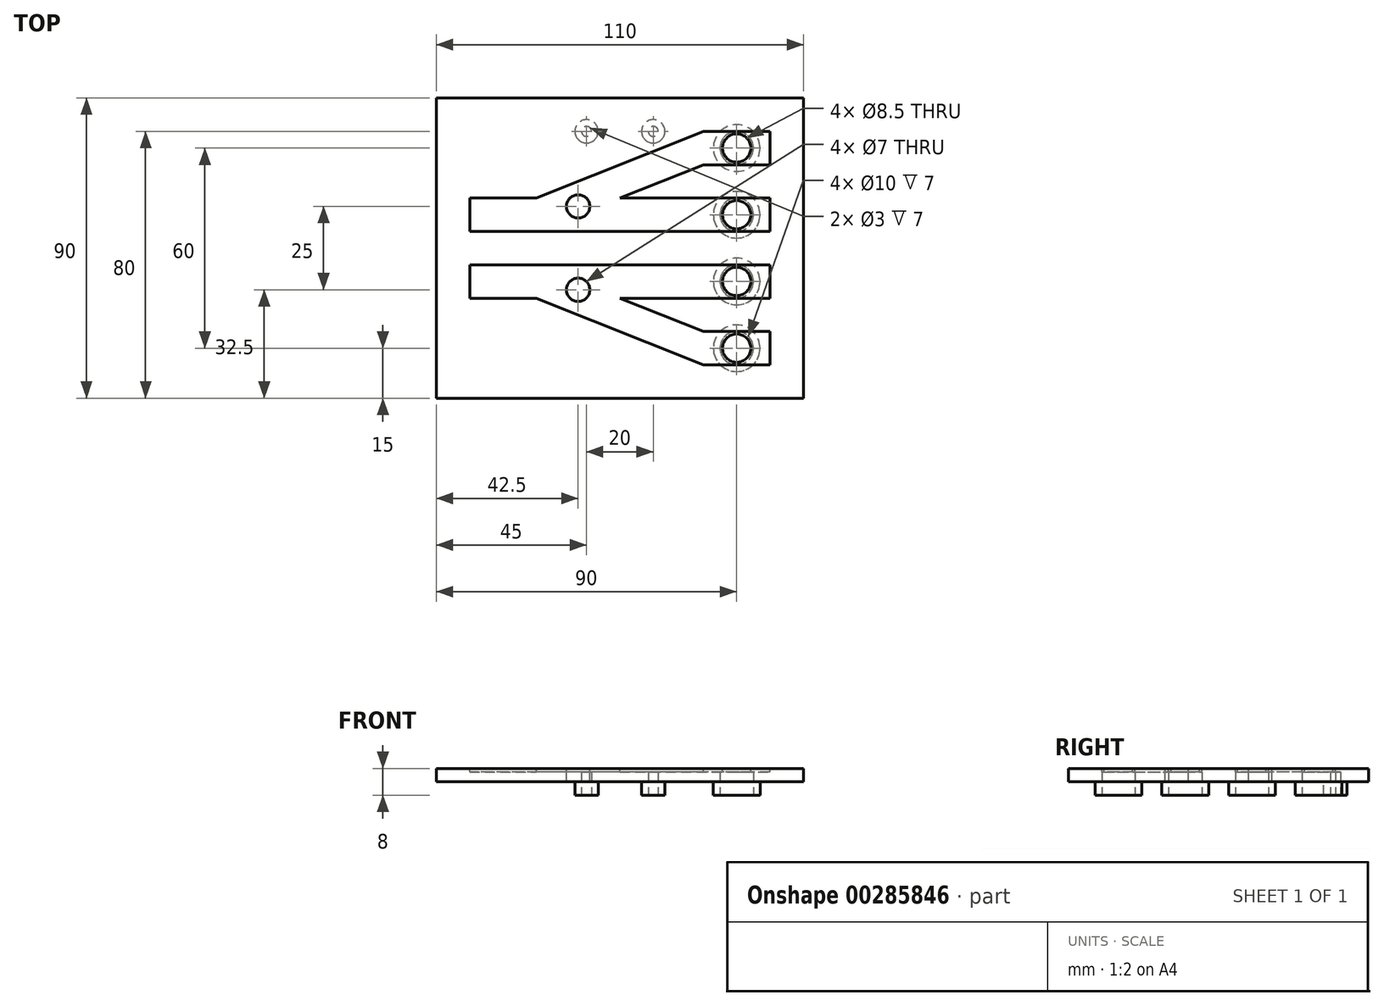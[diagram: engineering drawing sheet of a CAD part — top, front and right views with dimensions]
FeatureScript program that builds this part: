
annotation { "Feature Type Name" : "Feature", "Feature Type Description" : "" }
export const myFeature = defineFeature(function(context is Context, id is Id, definition is map)
    precondition{}
    {
        {
            var Q0;
            Q0=qCreatedBy(makeId("Top.planeOp"),FACE);
            var sketch = newSketch(context, id + "F0", { "sketchPlane" : qUnion([Q0])});
            skLineSegment(sketch, "E0.bottom", {"start": v(55, -45) * mm, "end": v(-55, -45) * mm});
            skLineSegment(sketch, "E0.top", {"start": v(55, 45) * mm, "end": v(-55, 45) * mm});
            skLineSegment(sketch, "E0.left", {"start": v(55, -45) * mm, "end": v(55, 45) * mm});
            skLineSegment(sketch, "E0.right", {"start": v(-55, -45) * mm, "end": v(-55, 45) * mm});
            skPoint(sketch, "E0.middle", {"position": v(0, 0) * mm});
            skSolve(sketch);
        }
        {
            var Q0;
            Q0 = qSketchRegion(id + "F0", true);
            extrude(context, id + "F1", {"entities" : qUnion([Q0]), "oppositeDirection" : true, "depth" : 4 * mm});
        }
        {
            var Q0;
            Q0=makeQuery(id+"F1.opExtrude","CAP_FACE",FACE,{"disambiguationData":[OSD([sQuery(id+"F0.wireOp",EDGE,"E0.bottom"),sQuery(id+"F0.wireOp",EDGE,"E0.top"),sQuery(id+"F0.wireOp",EDGE,"E0.left"),sQuery(id+"F0.wireOp",EDGE,"E0.right")])],"isStart":false});
            cPlane(context, id + "F2", {"entities" : qUnion([Q0]), "cplaneType" : CPlaneType.OFFSET, "offset" : 0 * mm, "width" : 150 * mm, "height" : 150 * mm});
        }
        {
            var Q0;
            Q0=qCreatedBy(makeId("Top.planeOp"),FACE);
            var sketch = newSketch(context, id + "F3", { "sketchPlane" : qUnion([Q0])});
            skLineSegment(sketch, "E1.bottom", {"start": v(-45, 15) * mm, "end": v(-25, 15) * mm});
            skLineSegment(sketch, "E1.left", {"start": v(-45, 15) * mm, "end": v(-45, 5) * mm});
            skLineSegment(sketch, "E1.right", {"start": v(45, 15) * mm, "end": v(45, 5) * mm});
            skLineSegment(sketch, "E2.bottom", {"start": v(45, 25) * mm, "end": v(25, 25) * mm});
            skLineSegment(sketch, "E2.top", {"start": v(45, 35) * mm, "end": v(25, 35) * mm});
            skLineSegment(sketch, "E2.left", {"start": v(45, 25) * mm, "end": v(45, 35) * mm});
            skLineSegment(sketch, "E3", {"start": v(25, 35) * mm, "end": v(-25, 15) * mm});
            skPoint(sketch, "E4.endSnap0", {"position": v(0, 25) * mm});
            skLineSegment(sketch, "E5", {"start": v(0, 15) * mm, "end": v(45, 15) * mm});
            skLineSegment(sketch, "E6", {"start": v(45, 5) * mm, "end": v(-45, 5) * mm});
            skPoint(sketch, "E7.startSnap0", {"position": v(0, 5) * mm});
            skLineSegment(sketch, "E8", {"start": v(25, 25) * mm, "end": v(0, 15) * mm});
            skPoint(sketch, "E9.centerSnap0", {"position": v(35, 35) * mm});
            skPoint(sketch, "E9.centerSnap1", {"position": v(45, 30) * mm});
            skPoint(sketch, "E10", {"position": v(45, 10) * mm});
            skLineSegment(sketch, "E11.MirrorCS", {"start": v(25, -25) * mm, "end": v(0, -15) * mm});
            skLineSegment(sketch, "E12.MirrorCS", {"start": v(45, -15) * mm, "end": v(45, -5) * mm});
            skLineSegment(sketch, "E13.MirrorCS", {"start": v(45, -35) * mm, "end": v(25, -35) * mm});
            skLineSegment(sketch, "E14.MirrorCS", {"start": v(-45, -15) * mm, "end": v(-25, -15) * mm});
            skLineSegment(sketch, "E15.MirrorCS", {"start": v(-45, -15) * mm, "end": v(-45, -5) * mm});
            skPoint(sketch, "E16.MirrorP", {"position": v(45, -30) * mm});
            skPoint(sketch, "E17.MirrorP", {"position": v(0, -25) * mm});
            skLineSegment(sketch, "E18.MirrorCS", {"start": v(45, -25) * mm, "end": v(25, -25) * mm});
            skLineSegment(sketch, "E19.MirrorCS", {"start": v(25, -35) * mm, "end": v(-25, -15) * mm});
            skLineSegment(sketch, "E20.MirrorCS", {"start": v(0, -15) * mm, "end": v(45, -15) * mm});
            skLineSegment(sketch, "E21.MirrorCS", {"start": v(45, -25) * mm, "end": v(45, -35) * mm});
            skLineSegment(sketch, "E22.MirrorCS", {"start": v(45, -5) * mm, "end": v(-45, -5) * mm});
            skPoint(sketch, "E23.MirrorP", {"position": v(0, -5) * mm});
            skPoint(sketch, "E24.MirrorP", {"position": v(45, -10) * mm});
            skPoint(sketch, "E25.MirrorP", {"position": v(35, -35) * mm});
            skSolve(sketch);
        }
        {
            var Q0;
            Q0=qCreatedBy(makeId("Top.planeOp"),FACE);
            var sketch = newSketch(context, id + "F4", { "sketchPlane" : qUnion([Q0])});
            skLineSegment(sketch, "E26.0.0", {"start": v(25, 25) * mm, "end": v(45, 25) * mm, "construction": true});
            skLineSegment(sketch, "E26.0.1", {"start": v(45, 25) * mm, "end": v(45, 35) * mm, "construction": true});
            skLineSegment(sketch, "E26.0.2", {"start": v(45, 35) * mm, "end": v(25, 35) * mm, "construction": true});
            skLineSegment(sketch, "E26.0.3", {"start": v(25, 35) * mm, "end": v(-25, 15) * mm, "construction": true});
            skLineSegment(sketch, "E26.0.4", {"start": v(-25, 15) * mm, "end": v(-45, 15) * mm, "construction": true});
            skLineSegment(sketch, "E26.0.5", {"start": v(-45, 15) * mm, "end": v(-45, 5) * mm, "construction": true});
            skLineSegment(sketch, "E26.0.6", {"start": v(-45, 5) * mm, "end": v(45, 5) * mm, "construction": true});
            skLineSegment(sketch, "E26.0.7", {"start": v(45, 5) * mm, "end": v(45, 15) * mm, "construction": true});
            skLineSegment(sketch, "E26.0.8", {"start": v(45, 15) * mm, "end": v(0, 15) * mm, "construction": true});
            skLineSegment(sketch, "E26.0.9", {"start": v(0, 15) * mm, "end": v(25, 25) * mm, "construction": true});
            skLineSegment(sketch, "E27.0.0", {"start": v(-45, -5) * mm, "end": v(-45, -15) * mm, "construction": true});
            skLineSegment(sketch, "E27.0.1", {"start": v(-45, -15) * mm, "end": v(-25, -15) * mm, "construction": true});
            skLineSegment(sketch, "E27.0.2", {"start": v(-25, -15) * mm, "end": v(25, -35) * mm, "construction": true});
            skLineSegment(sketch, "E27.0.3", {"start": v(25, -35) * mm, "end": v(45, -35) * mm, "construction": true});
            skLineSegment(sketch, "E27.0.4", {"start": v(45, -35) * mm, "end": v(45, -25) * mm, "construction": true});
            skLineSegment(sketch, "E27.0.5", {"start": v(45, -25) * mm, "end": v(25, -25) * mm, "construction": true});
            skLineSegment(sketch, "E27.0.6", {"start": v(25, -25) * mm, "end": v(0, -15) * mm, "construction": true});
            skLineSegment(sketch, "E27.0.7", {"start": v(0, -15) * mm, "end": v(45, -15) * mm, "construction": true});
            skLineSegment(sketch, "E27.0.8", {"start": v(45, -15) * mm, "end": v(45, -5) * mm, "construction": true});
            skLineSegment(sketch, "E27.0.9", {"start": v(45, -5) * mm, "end": v(-45, -5) * mm, "construction": true});
            skLineSegment(sketch, "E28", {"start": v(-25, 15) * mm, "end": v(0, 15) * mm, "construction": true});
            skLineSegment(sketch, "E29", {"start": v(-12.5, 5) * mm, "end": v(-12.5, 20) * mm, "construction": true});
            skPoint(sketch, "E29.startSnap0", {"position": v(-12.5, 15) * mm});
            skCircle(sketch, "E30", {"center": v(-12.5, 12.5) * mm, "radius": 3.5 * mm});
            skCircle(sketch, "E31", {"center": v(35, 30) * mm, "radius": 4.25 * mm});
            skPoint(sketch, "E31.centerSnap0", {"position": v(45, 30) * mm});
            skPoint(sketch, "E31.centerSnap1", {"position": v(35, 35) * mm});
            skCircle(sketch, "E32", {"center": v(35, 10) * mm, "radius": 4.25 * mm});
            skPoint(sketch, "E32.centerSnap0", {"position": v(45, 10) * mm});
            skPoint(sketch, "E32.centerSnap1", {"position": v(35, 25) * mm});
            skCircle(sketch, "E33.MirrorC", {"center": v(35, -10) * mm, "radius": 4.25 * mm});
            skCircle(sketch, "E34.MirrorC", {"center": v(35, -30) * mm, "radius": 4.25 * mm});
            skCircle(sketch, "E35.MirrorC", {"center": v(-12.5, -12.5) * mm, "radius": 3.5 * mm});
            skSolve(sketch);
        }
        {
            var Q0;
            Q0 = qSketchRegion(id + "F3", true);
            extrude(context, id + "F5", {"entities" : qUnion([Q0]), "operationType" : NewBodyOperationType.REMOVE, "oppositeDirection" : true, "depth" : 1 * mm});
        }
        {
            var Q0;
            Q0 = qSketchRegion(id + "F3", true);
            extrude(context, id + "F6", {"entities" : qUnion([Q0]), "oppositeDirection" : true, "depth" : 1 * mm});
        }
        {
            var Q0;
            Q0 = qSketchRegion(id + "F4", true);
            var Q1;
            Q1=makeQuery(id+"F1.opExtrude","CAP_FACE",FACE,{"disambiguationData":[OSD([sQuery(id+"F0.wireOp",EDGE,"E0.bottom"),sQuery(id+"F0.wireOp",EDGE,"E0.top"),sQuery(id+"F0.wireOp",EDGE,"E0.left"),sQuery(id+"F0.wireOp",EDGE,"E0.right")])],"isStart":false});
            extrude(context, id + "F7", {"entities" : qUnion([Q0]), "operationType" : NewBodyOperationType.REMOVE, "endBound" : BoundingType.UP_TO_SURFACE, "oppositeDirection" : true, "endBoundEntityFace" : qUnion([Q1]), "depth" : 25 * mm});
        }
        {
            var Q0;
            Q0=qCreatedBy(id+"F2.planeOp",FACE);
            var sketch = newSketch(context, id + "F8", { "sketchPlane" : qUnion([Q0])});
            skCircle(sketch, "E36.0", {"center": v(35, -30) * mm, "radius": 4.25 * mm, "construction": true});
            skCircle(sketch, "E37.0", {"center": v(35, -10) * mm, "radius": 4.25 * mm, "construction": true});
            skCircle(sketch, "E38.0", {"center": v(35, 10) * mm, "radius": 4.25 * mm, "construction": true});
            skCircle(sketch, "E39.0", {"center": v(35, 30) * mm, "radius": 4.25 * mm, "construction": true});
            skCircle(sketch, "E40", {"center": v(35, -30) * mm, "radius": 5 * mm});
            skCircle(sketch, "E41", {"center": v(35, -10) * mm, "radius": 5 * mm});
            skCircle(sketch, "E42", {"center": v(35, 10) * mm, "radius": 5 * mm});
            skCircle(sketch, "E43", {"center": v(35, 30) * mm, "radius": 5 * mm});
            skSolve(sketch);
        }
        {
            var Q0;
            Q0 = qSketchRegion(id + "F8", true);
            var Q1;
            Q1=makeQuery(id+"F6.opExtrude","CAP_FACE",FACE,{"disambiguationData":[OSD([sQuery(id+"F3.wireOp",EDGE,"E1.bottom"),sQuery(id+"F3.wireOp",EDGE,"E1.left"),sQuery(id+"F3.wireOp",EDGE,"E1.right"),sQuery(id+"F3.wireOp",EDGE,"E2.bottom"),sQuery(id+"F3.wireOp",EDGE,"E2.top"),sQuery(id+"F3.wireOp",EDGE,"E2.left"),sQuery(id+"F3.wireOp",EDGE,"E3"),sQuery(id+"F3.wireOp",EDGE,"E5"),sQuery(id+"F3.wireOp",EDGE,"E6"),sQuery(id+"F3.wireOp",EDGE,"E8")])],"isStart":false});
            extrude(context, id + "F9", {"entities" : qUnion([Q0]), "operationType" : NewBodyOperationType.REMOVE, "endBound" : BoundingType.UP_TO_SURFACE, "oppositeDirection" : true, "endBoundEntityFace" : qUnion([Q1]), "depth" : 25 * mm});
        }
        {
            var Q0;
            Q0=qCreatedBy(id+"F2.planeOp",FACE);
            var sketch = newSketch(context, id + "F10", { "sketchPlane" : qUnion([Q0])});
            skCircle(sketch, "E44.0", {"center": v(35, -30) * mm, "radius": 4.25 * mm, "construction": true});
            skCircle(sketch, "E45.0", {"center": v(35, -10) * mm, "radius": 4.25 * mm, "construction": true});
            skCircle(sketch, "E46.0", {"center": v(35, 10) * mm, "radius": 4.25 * mm, "construction": true});
            skCircle(sketch, "E47.0", {"center": v(35, 30) * mm, "radius": 4.25 * mm, "construction": true});
            skCircle(sketch, "E48", {"center": v(35, -30) * mm, "radius": 5 * mm});
            skCircle(sketch, "E49", {"center": v(35, -30) * mm, "radius": 7 * mm});
            skCircle(sketch, "E50", {"center": v(35, -10) * mm, "radius": 5 * mm});
            skCircle(sketch, "E51", {"center": v(35, -10) * mm, "radius": 7 * mm});
            skCircle(sketch, "E52", {"center": v(35, 10) * mm, "radius": 5 * mm});
            skCircle(sketch, "E53", {"center": v(35, 10) * mm, "radius": 7 * mm});
            skCircle(sketch, "E54", {"center": v(35, 30) * mm, "radius": 5 * mm});
            skCircle(sketch, "E55", {"center": v(35, 30) * mm, "radius": 7 * mm});
            skSolve(sketch);
        }
        {
            var Q0;
            Q0 = qSketchRegion(id + "F10", true);
            extrude(context, id + "F11", {"entities" : qUnion([Q0]), "operationType" : NewBodyOperationType.ADD, "depth" : 4 * mm});
        }
        {
            var Q0;
            Q0=qCreatedBy(id+"F2.planeOp",FACE);
            var sketch = newSketch(context, id + "F12", { "sketchPlane" : qUnion([Q0])});
            skLineSegment(sketch, "E56.0", {"start": v(55, -45) * mm, "end": v(-55, -45) * mm, "construction": true});
            skLineSegment(sketch, "E57", {"start": v(0, -45) * mm, "end": v(0, -35) * mm, "construction": true});
            skLineSegment(sketch, "E58", {"start": v(0, -35) * mm, "end": v(10, -35) * mm, "construction": true});
            skLineSegment(sketch, "E59", {"start": v(0, -35) * mm, "end": v(-10, -35) * mm, "construction": true});
            skCircle(sketch, "E60", {"center": v(10, -35) * mm, "radius": 3.5 * mm});
            skCircle(sketch, "E61", {"center": v(-10, -35) * mm, "radius": 3.5 * mm});
            skSolve(sketch);
        }
        {
            var Q0;
            Q0 = qSketchRegion(id + "F12", true);
            extrude(context, id + "F13", {"entities" : qUnion([Q0]), "operationType" : NewBodyOperationType.ADD, "depth" : 4 * mm});
        }
        {
            var Q0;
            Q0=makeQuery(id+"F13.opExtrude","CAP_FACE",FACE,{"disambiguationData":[OSD([sQuery(id+"F12.wireOp",EDGE,"E60")])],"isStart":false});
            cPlane(context, id + "F14", {"entities" : qUnion([Q0]), "cplaneType" : CPlaneType.OFFSET, "offset" : 0 * mm, "width" : 150 * mm, "height" : 150 * mm});
        }
        {
            var Q0;
            Q0=qCreatedBy(id+"F14.planeOp",FACE);
            var sketch = newSketch(context, id + "F15", { "sketchPlane" : qUnion([Q0])});
            skCircle(sketch, "E62.0.0", {"center": v(10, -35) * mm, "radius": 3.5 * mm, "construction": true});
            skCircle(sketch, "E63.0.0", {"center": v(-10, -35) * mm, "radius": 3.5 * mm, "construction": true});
            skCircle(sketch, "E64", {"center": v(10, -35) * mm, "radius": 1.5 * mm});
            skCircle(sketch, "E65", {"center": v(-10, -35) * mm, "radius": 1.5 * mm});
            skSolve(sketch);
        }
        {
            var Q0;
            Q0 = qSketchRegion(id + "F15", true);
            extrude(context, id + "F16", {"entities" : qUnion([Q0]), "operationType" : NewBodyOperationType.REMOVE, "oppositeDirection" : true, "depth" : 7 * mm});
        }
    });
